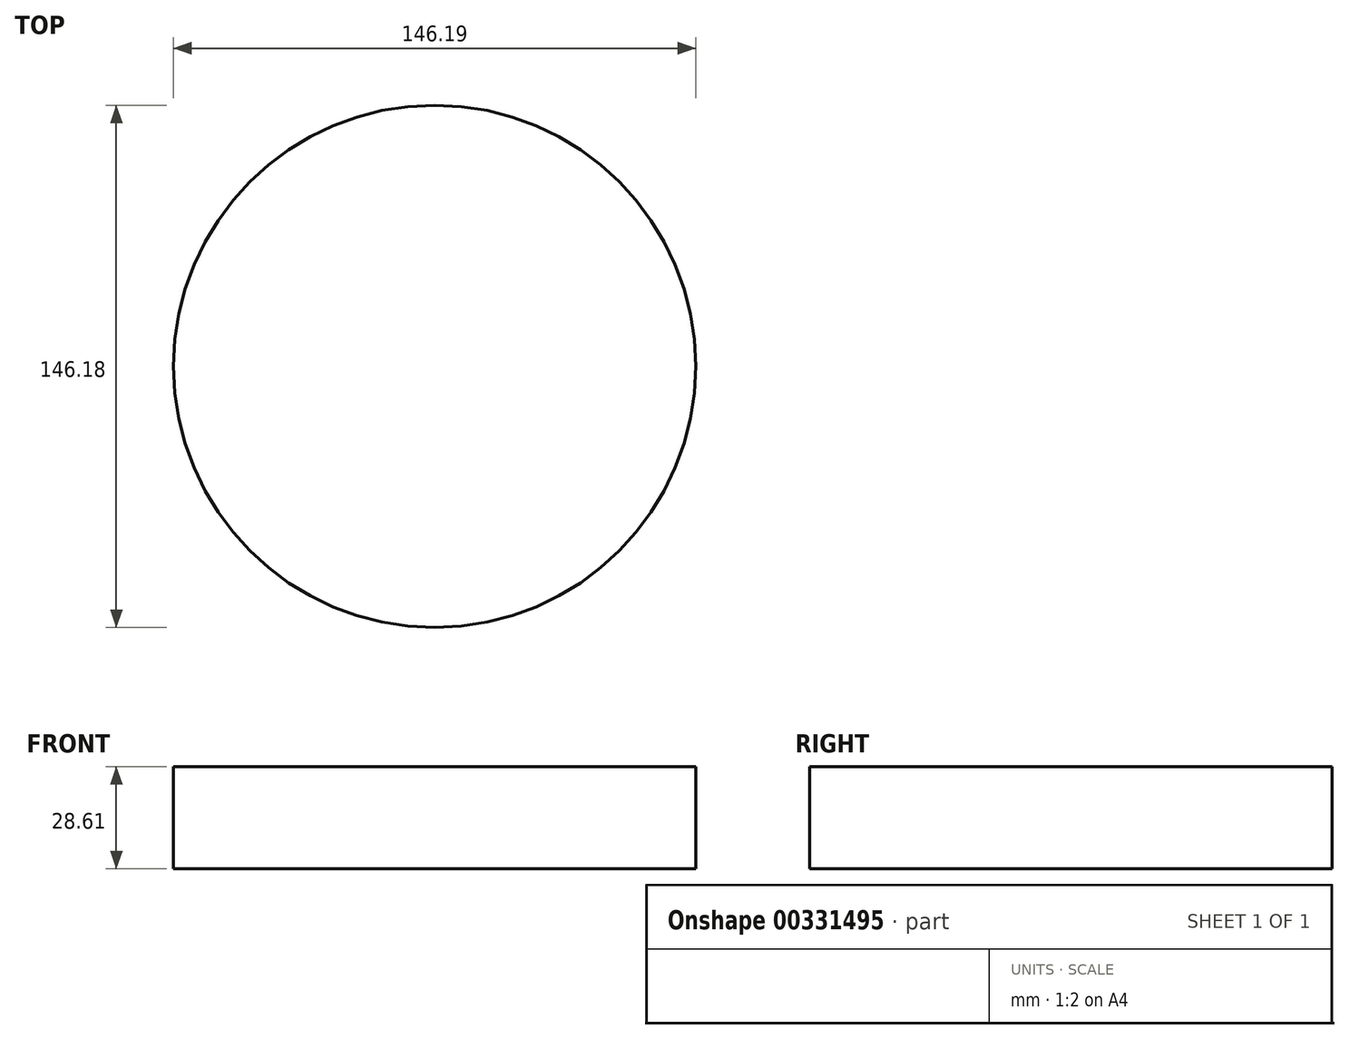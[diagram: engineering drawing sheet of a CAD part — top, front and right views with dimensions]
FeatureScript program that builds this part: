
annotation { "Feature Type Name" : "Feature", "Feature Type Description" : "" }
export const myFeature = defineFeature(function(context is Context, id is Id, definition is map)
    precondition{}
    {
        {
            var Q0;
            Q0=qCreatedBy(makeId("Top.planeOp"),FACE);
            var sketch = newSketch(context, id + "F0", { "sketchPlane" : qUnion([Q0])});
            skCircle(sketch, "E0", {"center": v(-29, 410.89) * mm, "radius": 73.1 * mm});
            skSolve(sketch);
        }
        {
            var Q0;
            Q0 = qSketchRegion(id + "F0", true);
            extrude(context, id + "F1", {"entities" : qUnion([Q0]), "depth" : 28.6 * mm});
        }
    });
